# Revit family: Hammereinsatz Typ 2536 für Staberder ST, BP und OMEX
name_source: partatom
category: Generic Models
revit_build: Autodesk Revit 2015 (Build: 20140606_1530(x64)
units: mm (PartAtom-declared; Revit-internal decimal feet)

## types (2) — shared parameters
Height = 212 mm  [stored 0.695538 ft]
Height 1 = 48 mm
Height 2 = 52 mm
Manufacturer = OBO Bettermann
Material = Steel
URL = http://www.obo-bettermann.com
Width = 15 mm
Width 2 = 9 mm  [stored 0.0295276 ft]

## per-type parameters (varying)
| type | GTIN | Manufacturer Art.No. | Width 1 |
| 2536 20 | 4012195643036 | 3044904 | 7 mm  [stored 0.0229659 ft] |
| 2536 25 | 4012195642978 | 3044831 | 8 mm  [stored 0.0262467 ft] |

note: column(s) folded — value = type name in every type: Article Type

note: [stored X ft] marks values corroborated as IEEE doubles in the binary element streams (Revit-internal decimal feet)

## geometry (parser evidence)
native form markers: Sweep x2
no freeform markers — native parametric forms only
